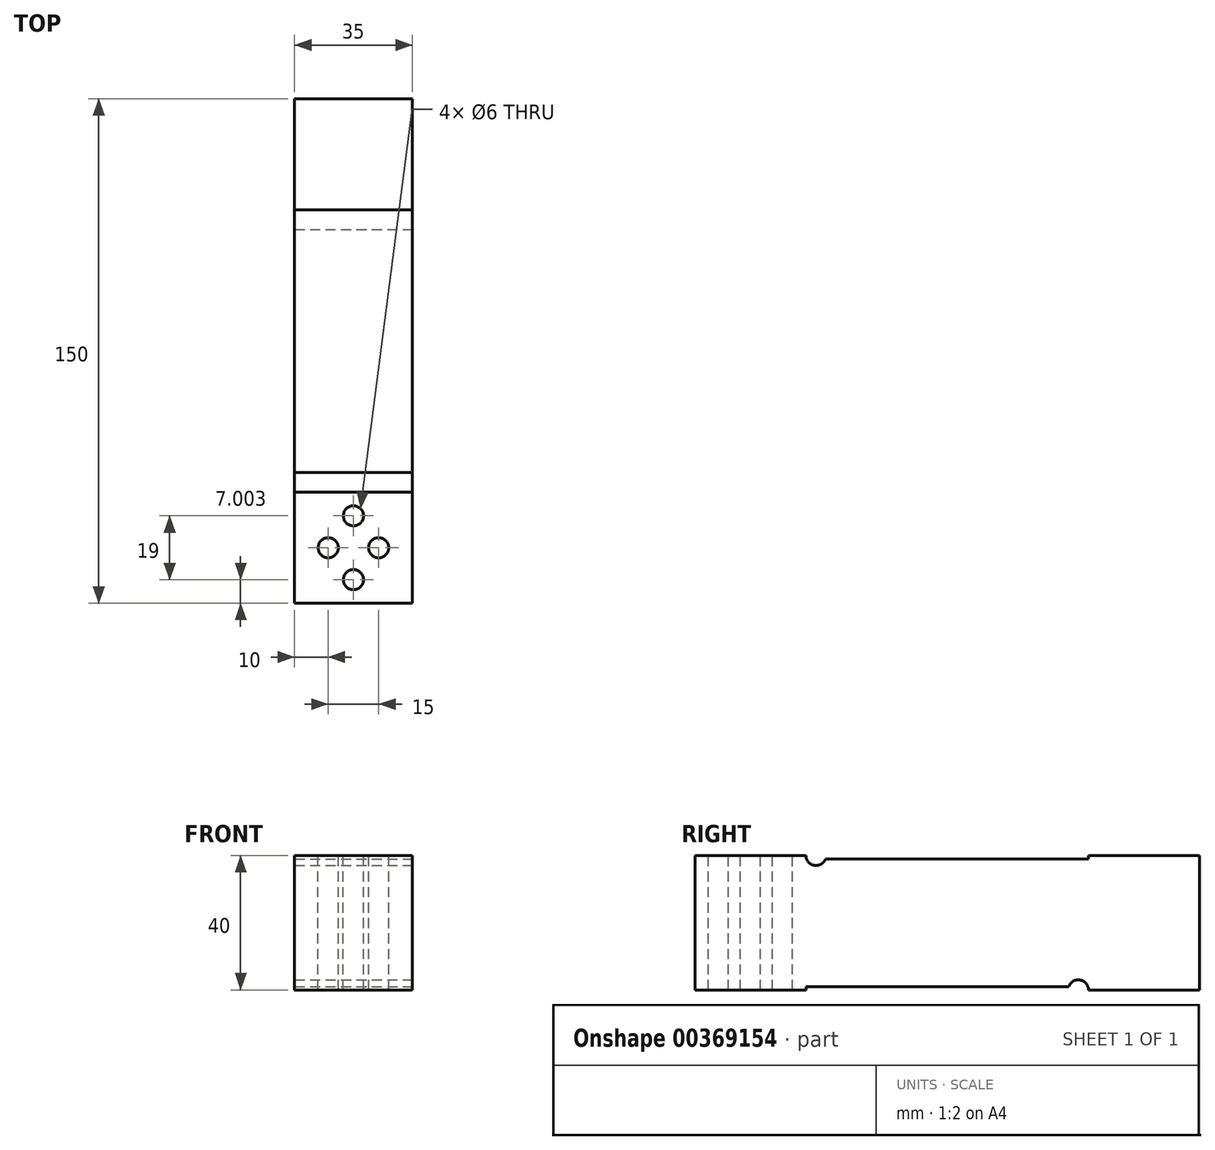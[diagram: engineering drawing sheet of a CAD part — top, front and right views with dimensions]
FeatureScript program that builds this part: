
annotation { "Feature Type Name" : "Feature", "Feature Type Description" : "" }
export const myFeature = defineFeature(function(context is Context, id is Id, definition is map)
    precondition{}
    {
        {
            var Q0;
            Q0=qCreatedBy(makeId("Top.planeOp"),FACE);
            var sketch = newSketch(context, id + "F0", { "sketchPlane" : qUnion([Q0])});
            skLineSegment(sketch, "E0.top", {"start": v(-17.5, 76.07) * mm, "end": v(17.5, 76.07) * mm});
            skLineSegment(sketch, "E0.left", {"start": v(-17.5, -73.93) * mm, "end": v(-17.5, 76.07) * mm});
            skLineSegment(sketch, "E0.right", {"start": v(17.5, -73.93) * mm, "end": v(17.5, 76.07) * mm});
            skLineSegment(sketch, "E1", {"start": v(-17.5, -73.93) * mm, "end": v(17.5, -73.93) * mm});
            skSolve(sketch);
        }
        {
            var Q0;
            Q0 = qSketchRegion(id + "F0", true);
            extrude(context, id + "F1", {"entities" : qUnion([Q0]), "endBound" : BoundingType.SYMMETRIC, "depth" : 40 * mm});
        }
        {
            var Q0;
            Q0=makeQuery(id+"F1.opExtrude","CAP_FACE",FACE,{"disambiguationData":[OSD([sQuery(id+"F0.wireOp",EDGE,"E0.top"),sQuery(id+"F0.wireOp",EDGE,"E0.left"),sQuery(id+"F0.wireOp",EDGE,"E0.right"),sQuery(id+"F0.wireOp",EDGE,"E1")])],"isStart":false});
            var sketch = newSketch(context, id + "F2", { "sketchPlane" : qUnion([Q0])});
            skPoint(sketch, "E2", {"position": v(0, -66.93) * mm});
            skPoint(sketch, "E3", {"position": v(0, -47.93) * mm});
            skPoint(sketch, "E4", {"position": v(7.5, -57.43) * mm});
            skPoint(sketch, "E5", {"position": v(-7.5, -57.43) * mm});
            skSolve(sketch);
        }
        {
            var Q0;
            Q0=sQuery(id+"F2.wireOp",VERTEX,"E2");
            var Q1;
            Q1=sQuery(id+"F2.wireOp",VERTEX,"E5");
            var Q2;
            Q2=sQuery(id+"F2.wireOp",VERTEX,"E3");
            var Q3;
            Q3=sQuery(id+"F2.wireOp",VERTEX,"E4");
            var Q4;
            Q4=makeQuery(id+"F1.opExtrude","SWEPT_BODY",BODY,{"disambiguationData":[OSD([sQuery(id+"F0.wireOp",EDGE,"E0.top"),sQuery(id+"F0.wireOp",EDGE,"E0.left"),sQuery(id+"F0.wireOp",EDGE,"E0.right"),sQuery(id+"F0.wireOp",EDGE,"E1")])]});
            hole(context, id + "F3", {"style" : HoleStyle.SIMPLE, "endStyle" : HoleEndStyle.THROUGH, "holeDiameter" : 6 * mm, "isTappedThrough" : true, "tappedDepth" : 12.7 * mm, "tapClearance" : 3, "locations" : qUnion([Q0, Q1, Q2, Q3]), "scope" : qUnion([Q4])});
        }
        {
            var Q0;
            Q0=qCreatedBy(makeId("Right.planeOp"),FACE);
            var sketch = newSketch(context, id + "F4", { "sketchPlane" : qUnion([Q0])});
            skArc(sketch, "E6", {"start": v(-37.82, 23) * mm, "mid": v(-40.4, 18.31) * mm, "end": v(-35.1, 19) * mm});
            skLineSegment(sketch, "E7", {"start": v(-35.1, 19) * mm, "end": v(43.07, 19) * mm});
            skLineSegment(sketch, "E8", {"start": v(43.07, 19) * mm, "end": v(43.07, 20) * mm});
            skLineSegment(sketch, "E9", {"start": v(43.07, 20) * mm, "end": v(-37.82, 23) * mm});
            skArc(sketch, "E10", {"start": v(39.96, -23) * mm, "mid": v(42.55, -18.31) * mm, "end": v(37.24, -19) * mm});
            skLineSegment(sketch, "E11", {"start": v(37.24, -19) * mm, "end": v(-40.93, -19) * mm});
            skLineSegment(sketch, "E12", {"start": v(-40.93, -19) * mm, "end": v(-40.93, -20) * mm});
            skLineSegment(sketch, "E13", {"start": v(-40.93, -20) * mm, "end": v(39.96, -23) * mm});
            skSolve(sketch);
        }
        {
            var Q0;
            Q0 = qSketchRegion(id + "F4", true);
            extrude(context, id + "F5", {"entities" : qUnion([Q0]), "operationType" : NewBodyOperationType.REMOVE, "endBound" : BoundingType.SYMMETRIC, "oppositeDirection" : true, "depth" : 50 * mm});
        }
    });
